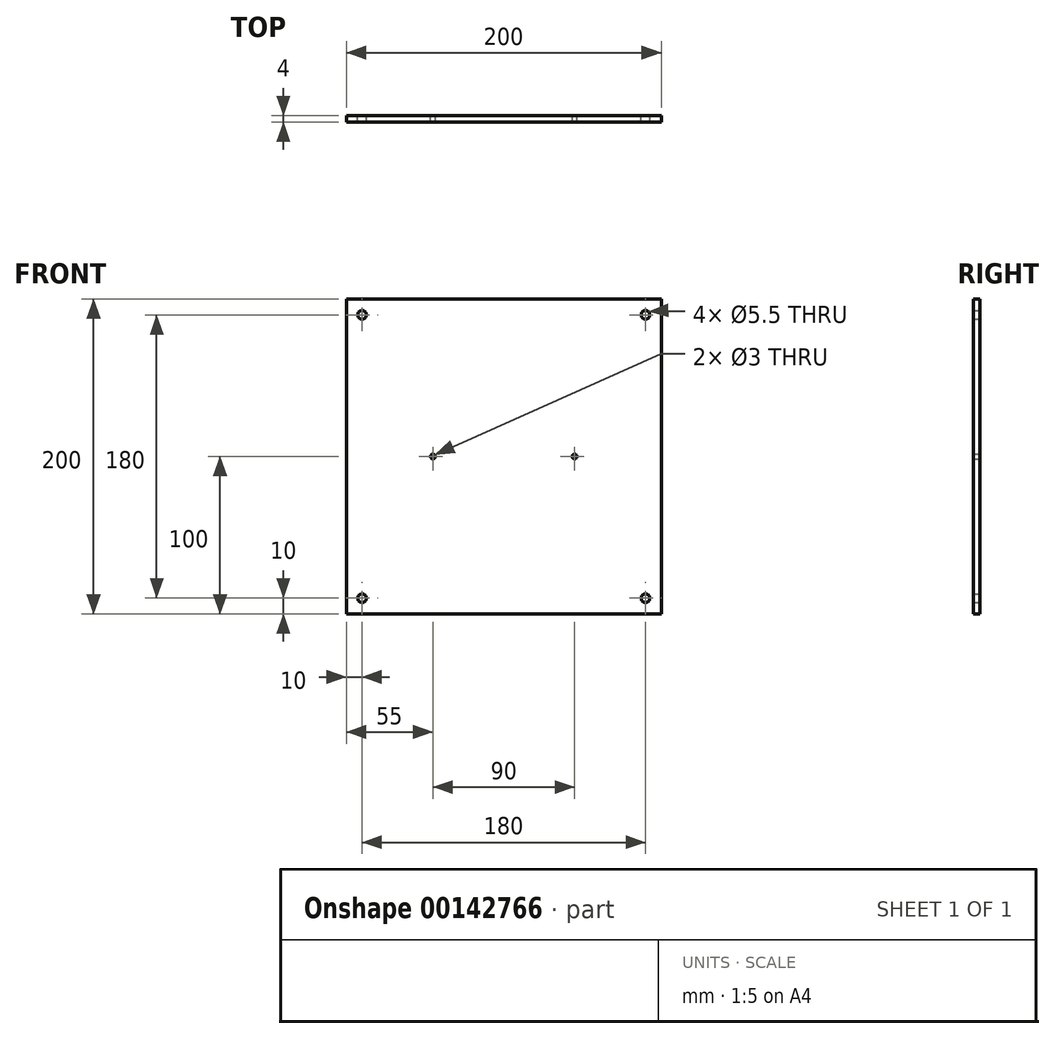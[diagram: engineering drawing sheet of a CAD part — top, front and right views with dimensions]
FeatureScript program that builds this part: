
annotation { "Feature Type Name" : "Feature", "Feature Type Description" : "" }
export const myFeature = defineFeature(function(context is Context, id is Id, definition is map)
    precondition{}
    {
        {
            var Q0;
            Q0=qCreatedBy(makeId("Front.planeOp"),FACE);
            var sketch = newSketch(context, id + "F0", { "sketchPlane" : qUnion([Q0])});
            skLineSegment(sketch, "E0.bottom", {"start": v(-100, -100) * mm, "end": v(100, -100) * mm});
            skLineSegment(sketch, "E0.top", {"start": v(-100, 100) * mm, "end": v(100, 100) * mm});
            skLineSegment(sketch, "E0.left", {"start": v(-100, -100) * mm, "end": v(-100, 100) * mm});
            skLineSegment(sketch, "E0.right", {"start": v(100, -100) * mm, "end": v(100, 100) * mm});
            skPoint(sketch, "E0.middle", {"position": v(0, 0) * mm});
            skCircle(sketch, "E1", {"center": v(-90, 90) * mm, "radius": 2.75 * mm});
            skCircle(sketch, "E2", {"center": v(90, 90) * mm, "radius": 2.75 * mm});
            skCircle(sketch, "E3", {"center": v(-90, -90) * mm, "radius": 2.75 * mm});
            skCircle(sketch, "E4", {"center": v(90, -90) * mm, "radius": 2.75 * mm});
            skCircle(sketch, "E5", {"center": v(45, 0) * mm, "radius": 1.5 * mm});
            skCircle(sketch, "E6", {"center": v(-45, 0) * mm, "radius": 1.5 * mm});
            skSolve(sketch);
        }
        {
            var Q0;
            Q0=makeQuery(id+"F0.imprint","IMPRINT",FACE,{"disambiguationData":[TD([[makeQuery(id+"F0.imprint","IMPRINT",EDGE,{"derivedFrom":sQuery(id+"F0.wireOp",EDGE,"E0.bottom")}),1.0]])]});
            extrude(context, id + "F1", {"entities" : qUnion([Q0]), "depth" : 4 * mm});
        }
    });
